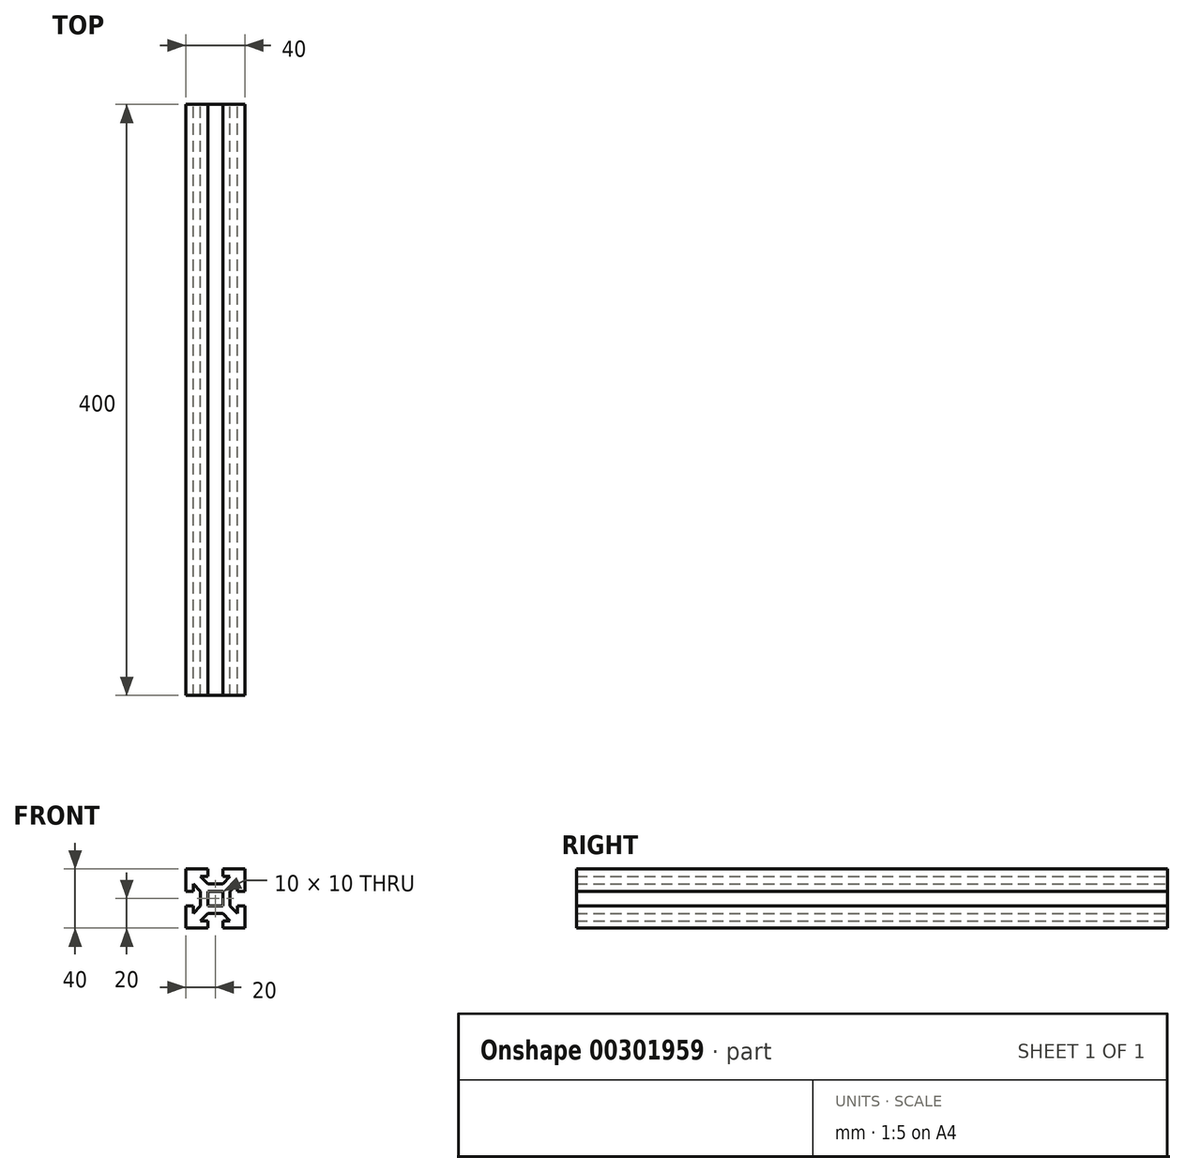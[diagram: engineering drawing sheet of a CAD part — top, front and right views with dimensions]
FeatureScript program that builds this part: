
annotation { "Feature Type Name" : "Feature", "Feature Type Description" : "" }
export const myFeature = defineFeature(function(context is Context, id is Id, definition is map)
    precondition{}
    {
        {
            var Q0;
            Q0=qCreatedBy(makeId("Front.planeOp"),FACE);
            var sketch = newSketch(context, id + "F0", { "sketchPlane" : qUnion([Q0])});
            skLineSegment(sketch, "E0.bottom", {"start": v(20, 20) * mm, "end": v(5, 20) * mm});
            skLineSegment(sketch, "E0.top", {"start": v(20, -20) * mm, "end": v(5, -20) * mm});
            skLineSegment(sketch, "E0.left", {"start": v(20, 20) * mm, "end": v(20, 5) * mm});
            skLineSegment(sketch, "E0.right", {"start": v(-20, 20) * mm, "end": v(-20, 5) * mm});
            skPoint(sketch, "E0.middle", {"position": v(0, 0) * mm});
            skLineSegment(sketch, "E1", {"start": v(0, 20) * mm, "end": v(0, -20) * mm, "construction": true});
            skLineSegment(sketch, "E2", {"start": v(-20, 0) * mm, "end": v(20, 0) * mm, "construction": true});
            skLineSegment(sketch, "E3", {"start": v(-20, 5) * mm, "end": v(-15, 5) * mm});
            skLineSegment(sketch, "E4", {"start": v(-20, -5) * mm, "end": v(-15, -5) * mm});
            skLineSegment(sketch, "E5", {"start": v(-5, 20) * mm, "end": v(-5, 15) * mm});
            skLineSegment(sketch, "E6", {"start": v(5, 20) * mm, "end": v(5, 15) * mm});
            skLineSegment(sketch, "E7", {"start": v(-10, 15) * mm, "end": v(-5, 15) * mm});
            skLineSegment(sketch, "E8", {"start": v(-10, -15) * mm, "end": v(-5, -15) * mm});
            skLineSegment(sketch, "E9", {"start": v(15, 10) * mm, "end": v(15, 5) * mm});
            skLineSegment(sketch, "E10", {"start": v(-15, 10) * mm, "end": v(-10, 5) * mm});
            skLineSegment(sketch, "E11", {"start": v(-10, 15) * mm, "end": v(-5, 10) * mm});
            skLineSegment(sketch, "E12", {"start": v(-15, -10) * mm, "end": v(-10, -5) * mm});
            skLineSegment(sketch, "E13", {"start": v(-10, -15) * mm, "end": v(-5, -10) * mm});
            skLineSegment(sketch, "E14.trimOffspring", {"start": v(20, -5) * mm, "end": v(20, -20) * mm});
            skLineSegment(sketch, "E15.trimOffspring", {"start": v(-20, -5) * mm, "end": v(-20, -20) * mm});
            skLineSegment(sketch, "E16.trimOffspring", {"start": v(-5, -20) * mm, "end": v(-20, -20) * mm});
            skLineSegment(sketch, "E17.trimOffspring", {"start": v(-5, 20) * mm, "end": v(-20, 20) * mm});
            skLineSegment(sketch, "E18.trimOffspring", {"start": v(5, 15) * mm, "end": v(10, 15) * mm});
            skLineSegment(sketch, "E19.trimOffspring", {"start": v(-15, -5) * mm, "end": v(-15, -10) * mm});
            skLineSegment(sketch, "E20.trimOffspring", {"start": v(15, -5) * mm, "end": v(15, -10) * mm});
            skLineSegment(sketch, "E21.trimOffspring", {"start": v(5, -15) * mm, "end": v(10, -15) * mm});
            skLineSegment(sketch, "E22.trimOffspring", {"start": v(-5, 5) * mm, "end": v(-5, -5) * mm});
            skLineSegment(sketch, "E23.trimOffspring", {"start": v(5, 5) * mm, "end": v(5, -5) * mm});
            skLineSegment(sketch, "E24.trimOffspring", {"start": v(15, 5) * mm, "end": v(20, 5) * mm});
            skLineSegment(sketch, "E25.trimOffspring", {"start": v(15, -5) * mm, "end": v(20, -5) * mm});
            skLineSegment(sketch, "E26.trimOffspring", {"start": v(5, -15) * mm, "end": v(5, -20) * mm});
            skLineSegment(sketch, "E27.trimOffspring", {"start": v(-5, -15) * mm, "end": v(-5, -20) * mm});
            skLineSegment(sketch, "E28.trimOffspring", {"start": v(-5, -5) * mm, "end": v(5, -5) * mm});
            skLineSegment(sketch, "E29.trimOffspring", {"start": v(-5, 5) * mm, "end": v(5, 5) * mm});
            skLineSegment(sketch, "E30", {"start": v(10, 5) * mm, "end": v(10, -5) * mm});
            skLineSegment(sketch, "E31", {"start": v(-5, 10) * mm, "end": v(5, 10) * mm});
            skLineSegment(sketch, "E32", {"start": v(-10, 5) * mm, "end": v(-10, -5) * mm});
            skLineSegment(sketch, "E33", {"start": v(-5, -10) * mm, "end": v(5, -10) * mm});
            skLineSegment(sketch, "E34.trimOffspring", {"start": v(-15, 10) * mm, "end": v(-15, 5) * mm});
            skPoint(sketch, "E35.orphan", {"position": v(20, 15) * mm});
            skPoint(sketch, "E36.orphan", {"position": v(20, -15) * mm});
            skPoint(sketch, "E37.orphan", {"position": v(15, -20) * mm});
            skPoint(sketch, "E38.orphan", {"position": v(-15, -20) * mm});
            skLineSegment(sketch, "E39.trimOffspring", {"start": v(-5, 0) * mm, "end": v(0, -5) * mm});
            skLineSegment(sketch, "E40.trimOffspring", {"start": v(-5, 0) * mm, "end": v(0, 5) * mm});
            skLineSegment(sketch, "E41.trimOffspring", {"start": v(0, 5) * mm, "end": v(5, 0) * mm});
            skLineSegment(sketch, "E42.trimOffspring", {"start": v(5, 10) * mm, "end": v(10, 15) * mm});
            skLineSegment(sketch, "E43.trimOffspring", {"start": v(10, 5) * mm, "end": v(15, 10) * mm});
            skLineSegment(sketch, "E44.trimOffspring", {"start": v(10, -5) * mm, "end": v(15, -10) * mm});
            skLineSegment(sketch, "E45.trimOffspring", {"start": v(5, -10) * mm, "end": v(10, -15) * mm});
            skLineSegment(sketch, "E46.trimOffspring", {"start": v(0, -5) * mm, "end": v(5, 0) * mm});
            skSolve(sketch);
        }
        {
            var Q0;
            Q0=makeQuery(id+"F0.imprint","IMPRINT",FACE,{"disambiguationData":[TD([[makeQuery(id+"F0.imprint","IMPRINT",EDGE,{"derivedFrom":sQuery(id+"F0.wireOp",EDGE,"E0.bottom")}),1.0]])]});
            extrude(context, id + "F1", {"entities" : qUnion([Q0]), "depth" : 400 * mm});
        }
    });
